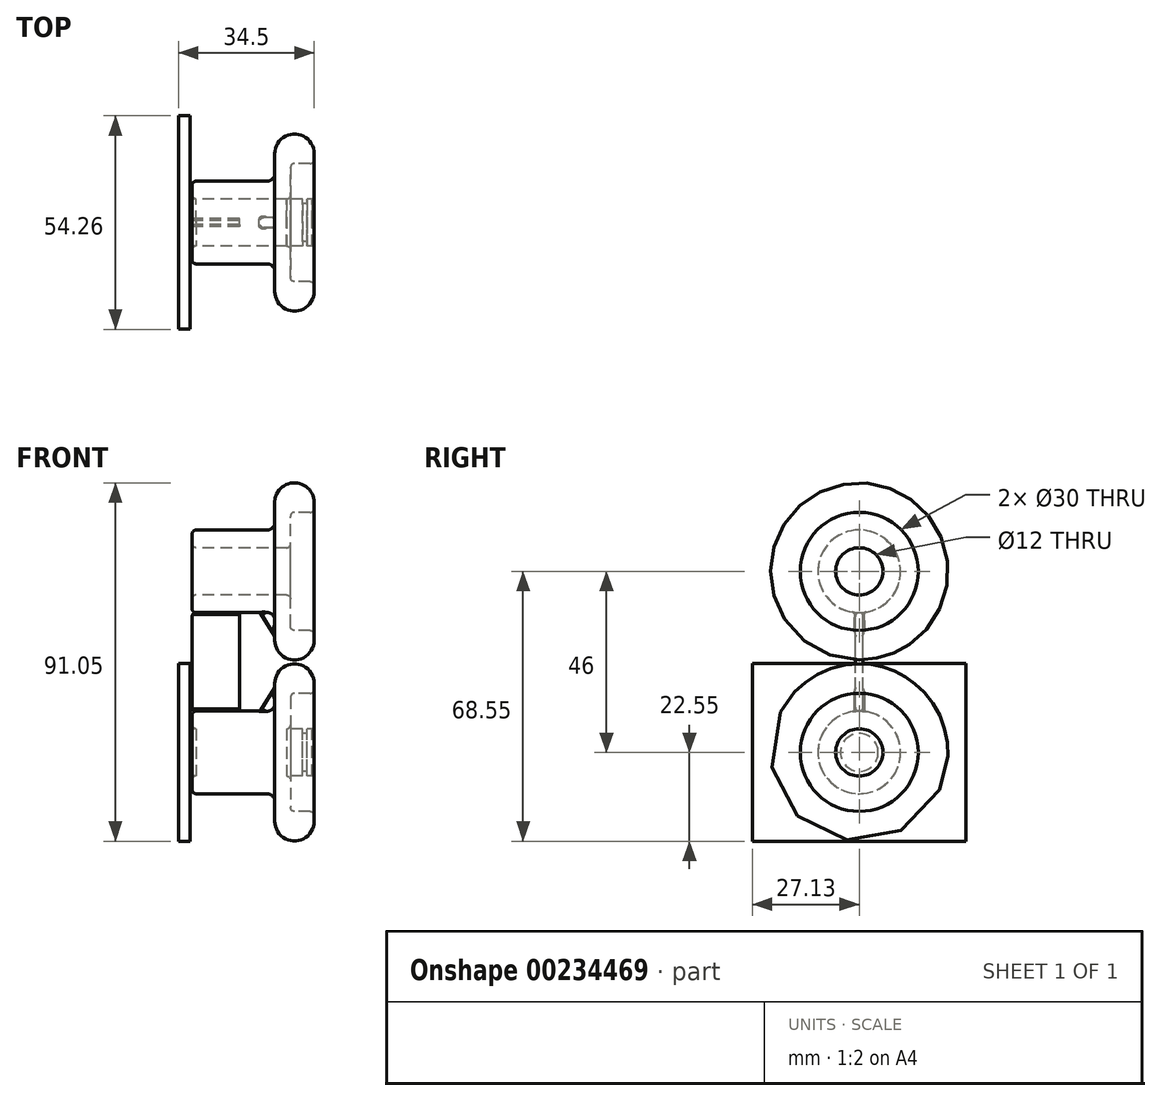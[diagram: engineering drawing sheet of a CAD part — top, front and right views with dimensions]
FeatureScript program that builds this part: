
annotation { "Feature Type Name" : "Feature", "Feature Type Description" : "" }
export const myFeature = defineFeature(function(context is Context, id is Id, definition is map)
    precondition{}
    {
        {
            var Q0;
            Q0=qCreatedBy(makeId("Right.planeOp"),FACE);
            var sketch = newSketch(context, id + "F0", { "sketchPlane" : qUnion([Q0])});
            skCircle(sketch, "E0", {"center": v(0, 0) * mm, "radius": 6 * mm});
            skSolve(sketch);
        }
        {
            var Q0;
            Q0 = qSketchRegion(id + "F0", true);
            extrude(context, id + "F1", {"entities" : qUnion([Q0]), "depth" : 31 * mm});
        }
        {
            var Q0;
            Q0=makeQuery(id+"F1.opExtrude","CAP_FACE",FACE,{"disambiguationData":[OSD([sQuery(id+"F0.wireOp",EDGE,"E0")])],"isStart":true});
            var sketch = newSketch(context, id + "F2", { "sketchPlane" : qUnion([Q0])});
            skLineSegment(sketch, "E1.bottom", {"start": v(-27.13, 22.55) * mm, "end": v(27.13, 22.55) * mm});
            skLineSegment(sketch, "E1.top", {"start": v(-27.13, -22.55) * mm, "end": v(27.13, -22.55) * mm});
            skLineSegment(sketch, "E1.left", {"start": v(-27.13, 22.55) * mm, "end": v(-27.13, -22.55) * mm});
            skLineSegment(sketch, "E1.right", {"start": v(27.13, 22.55) * mm, "end": v(27.13, -22.55) * mm});
            skPoint(sketch, "E1.middle", {"position": v(0, 0) * mm});
            skSolve(sketch);
        }
        {
            var Q0;
            Q0 = qSketchRegion(id + "F2", true);
            extrude(context, id + "F3", {"entities" : qUnion([Q0]), "operationType" : NewBodyOperationType.ADD, "depth" : 3 * mm});
        }
        {
            var Q0;
            Q0=qCreatedBy(makeId("Right.planeOp"),FACE);
            cPlane(context, id + "F4", {"entities" : qUnion([Q0]), "cplaneType" : CPlaneType.OFFSET, "offset" : 28.5 * mm, "width" : 150 * mm, "height" : 150 * mm});
        }
        {
            var Q0;
            Q0=qCreatedBy(id+"F4.planeOp",FACE);
            var sketch = newSketch(context, id + "F5", { "sketchPlane" : qUnion([Q0])});
            skCircle(sketch, "E2.0", {"center": v(0, 0) * mm, "radius": 6 * mm});
            skCircle(sketch, "E3", {"center": v(0, 0) * mm, "radius": 4.8 * mm});
            skSolve(sketch);
        }
        {
            var Q0;
            Q0 = qSketchRegion(id + "F5", true);
            extrude(context, id + "F6", {"entities" : qUnion([Q0]), "operationType" : NewBodyOperationType.REMOVE, "depth" : 1.2 * mm});
        }
        {
            var Q0;
            Q0=qCreatedBy(makeId("Front.planeOp"),FACE);
            var sketch = newSketch(context, id + "F7", { "sketchPlane" : qUnion([Q0])});
            skLineSegment(sketch, "E4", {"start": v(0.5, 6) * mm, "end": v(25.5, 6) * mm});
            skLineSegment(sketch, "E5", {"start": v(25.5, 6) * mm, "end": v(25.5, 15) * mm});
            skLineSegment(sketch, "E6", {"start": v(25.5, 15) * mm, "end": v(31.5, 15) * mm});
            skLineSegment(sketch, "E7", {"start": v(31.5, 15) * mm, "end": v(31.5, 17.5) * mm});
            skArc(sketch, "E8", {"start": v(31.5, 17.5) * mm, "mid": v(26.5, 22.5) * mm, "end": v(21.5, 17.5) * mm});
            skLineSegment(sketch, "E9", {"start": v(21.5, 17.5) * mm, "end": v(21.5, 10.5) * mm});
            skLineSegment(sketch, "E10", {"start": v(21.5, 10.5) * mm, "end": v(0.5, 10.5) * mm});
            skLineSegment(sketch, "E11", {"start": v(0.5, 10.5) * mm, "end": v(0.5, 6) * mm});
            skLineSegment(sketch, "E12", {"start": v(0, 0) * mm, "end": v(43.23, 0) * mm, "construction": true});
            skSolve(sketch);
        }
        {
            var Q0;
            Q0 = qSketchRegion(id + "F7", true);
            var Q1;
            Q1=sQuery(id+"F7.wireOp",EDGE,"E12");
            revolve(context, id + "F8", {"entities" : qUnion([Q0]), "axis" : qUnion([Q1]), "revolveType" : RevolveType.FULL});
        }
        {
            var Q0;
            Q0=qCreatedBy(makeId("Front.planeOp"),FACE);
            var sketch = newSketch(context, id + "F9", { "sketchPlane" : qUnion([Q0])});
            skLineSegment(sketch, "E13", {"start": v(17.5, 10.5) * mm, "end": v(21.5, 10.5) * mm, "construction": true});
            skLineSegment(sketch, "E14.0", {"start": v(21.5, 10.5) * mm, "end": v(21.5, 16.5) * mm});
            skPoint(sketch, "E15.orphan", {"position": v(21.5, 17.5) * mm});
            skPoint(sketch, "E16.orphan", {"position": v(21.5, -17.5) * mm});
            skLineSegment(sketch, "E17", {"start": v(17.5, 10.5) * mm, "end": v(17.5, 10) * mm, "construction": true});
            skLineSegment(sketch, "E18", {"start": v(17.5, 10) * mm, "end": v(21.5, 10) * mm});
            skLineSegment(sketch, "E19", {"start": v(21.5, 10) * mm, "end": v(21.5, 10.5) * mm});
            skLineSegment(sketch, "E20", {"start": v(21.5, 16.5) * mm, "end": v(17.5, 10) * mm});
            skSolve(sketch);
        }
        {
            var Q0;
            Q0 = qSketchRegion(id + "F9", true);
            extrude(context, id + "F10", {"entities" : qUnion([Q0]), "operationType" : NewBodyOperationType.ADD, "depth" : 2.5 * mm, "symmetric" : true});
        }
        {
            var Q0;
            Q0=makeQuery(id+"F8.opRevolve","SWEPT_EDGE",EDGE,{"disambiguationData":[OSD([sQuery(id+"F7.wireOp",EDGE,"E10"),sQuery(id+"F7.wireOp",EDGE,"E11")])]});
            var Q1;
            Q1=makeQuery(id+"F8.opRevolve","SWEPT_EDGE",EDGE,{"disambiguationData":[OSD([sQuery(id+"F7.wireOp",EDGE,"E6"),sQuery(id+"F7.wireOp",EDGE,"E7")])]});
            var Q2;
            Q2=makeQuery(id+"F8.opRevolve","SWEPT_EDGE",EDGE,{"disambiguationData":[OSD([sQuery(id+"F7.wireOp",EDGE,"E5"),sQuery(id+"F7.wireOp",EDGE,"E6")])]});
            var Q3;
            Q3=makeQuery(id+"F8.opRevolve","SWEPT_EDGE",EDGE,{"disambiguationData":[OSD([sQuery(id+"F7.wireOp",EDGE,"E4"),sQuery(id+"F7.wireOp",EDGE,"E5")])]});
            var Q4;
            Q4=makeQuery(id+"F8.opRevolve","SWEPT_EDGE",EDGE,{"disambiguationData":[OSD([sQuery(id+"F7.wireOp",EDGE,"E4"),sQuery(id+"F7.wireOp",EDGE,"E11")])]});
            fillet(context, id + "F11", {"entities" : qUnion([Q0, Q1, Q2, Q3, Q4]), "radius" : 1 * mm, "tangentPropagation" : true, "allowEdgeOverflow" : false});
        }
        {
            var Q0;
            {var subQ0=sQuery(id+"F7.wireOp",EDGE,"E9");var subQ2=sQuery(id+"F7.wireOp",EDGE,"E10");var subQ4=sQuery(id+"F9.wireOp",EDGE,"E19");var subQ5=sQuery(id+"F9.wireOp",EDGE,"E18");var subQ6=sQuery(id+"F9.wireOp",EDGE,"E17");var subQ7=sQuery(id+"F9.wireOp",EDGE,"57NRQQfy-ApiX-kUXl-zlCa-fPG9OK4gbSLN");var subQ8=sQuery(id+"F9.wireOp",EDGE,"E14.0");var subQ9=makeQuery(id+"FuQiQC3kxtkCGsf_2.5.F10.opExtrude","CAP_FACE",FACE,{"disambiguationData":[OSD([subQ8,subQ7,subQ6,subQ5,subQ4])],"isStart":true});var subQ10=makeQuery(id+"F10.opExtrude","CAP_FACE",FACE,{"disambiguationData":[OSD([subQ8,subQ7,subQ6,subQ5,subQ4])],"isStart":false});Q0=makeQuery(id+"FuQiQC3kxtkCGsf_2.6.F10.boolean.opBoolean","SPLIT",EDGE,{"disambiguationData":[TD([subQ9])],"derivedFrom":makeQuery(id+"FuQiQC3kxtkCGsf_2.5.F10.boolean.opBoolean","SPLIT",EDGE,{"disambiguationData":[TD([subQ10])],"derivedFrom":makeQuery(id+"FuQiQC3kxtkCGsf_2.4.F10.boolean.opBoolean","SPLIT",EDGE,{"disambiguationData":[TD([subQ10])],"derivedFrom":makeQuery(id+"FuQiQC3kxtkCGsf_2.3.F10.boolean.opBoolean","SPLIT",EDGE,{"disambiguationData":[TD([subQ10])],"derivedFrom":makeQuery(id+"FuQiQC3kxtkCGsf_2.2.F10.boolean.opBoolean","SPLIT",EDGE,{"disambiguationData":[TD([subQ10])],"derivedFrom":makeQuery(id+"FuQiQC3kxtkCGsf_2.1.F10.boolean.opBoolean","SPLIT",EDGE,{"disambiguationData":[TD([subQ10])],"derivedFrom":makeQuery(id+"F8.opRevolve","SWEPT_EDGE",EDGE,{"disambiguationData":[OSD([subQ0,subQ2])]})})})})})})});}
            var Q1;
            {var subQ0=sQuery(id+"F7.wireOp",EDGE,"E9");var subQ2=sQuery(id+"F7.wireOp",EDGE,"E10");var subQ4=sQuery(id+"F9.wireOp",EDGE,"E19");var subQ5=sQuery(id+"F9.wireOp",EDGE,"E18");var subQ6=sQuery(id+"F9.wireOp",EDGE,"E17");var subQ7=sQuery(id+"F9.wireOp",EDGE,"57NRQQfy-ApiX-kUXl-zlCa-fPG9OK4gbSLN");var subQ8=sQuery(id+"F9.wireOp",EDGE,"E14.0");var subQ9=makeQuery(id+"FuQiQC3kxtkCGsf_2.6.F10.opExtrude","CAP_FACE",FACE,{"disambiguationData":[OSD([subQ8,subQ7,subQ6,subQ5,subQ4])],"isStart":true});var subQ10=makeQuery(id+"F10.opExtrude","CAP_FACE",FACE,{"disambiguationData":[OSD([subQ8,subQ7,subQ6,subQ5,subQ4])],"isStart":false});Q1=makeQuery(id+"FuQiQC3kxtkCGsf_2.7.F10.boolean.opBoolean","SPLIT",EDGE,{"disambiguationData":[TD([subQ9])],"derivedFrom":makeQuery(id+"FuQiQC3kxtkCGsf_2.6.F10.boolean.opBoolean","SPLIT",EDGE,{"disambiguationData":[TD([subQ10])],"derivedFrom":makeQuery(id+"FuQiQC3kxtkCGsf_2.5.F10.boolean.opBoolean","SPLIT",EDGE,{"disambiguationData":[TD([subQ10])],"derivedFrom":makeQuery(id+"FuQiQC3kxtkCGsf_2.4.F10.boolean.opBoolean","SPLIT",EDGE,{"disambiguationData":[TD([subQ10])],"derivedFrom":makeQuery(id+"FuQiQC3kxtkCGsf_2.3.F10.boolean.opBoolean","SPLIT",EDGE,{"disambiguationData":[TD([subQ10])],"derivedFrom":makeQuery(id+"FuQiQC3kxtkCGsf_2.2.F10.boolean.opBoolean","SPLIT",EDGE,{"disambiguationData":[TD([subQ10])],"derivedFrom":makeQuery(id+"FuQiQC3kxtkCGsf_2.1.F10.boolean.opBoolean","SPLIT",EDGE,{"disambiguationData":[TD([subQ10])],"derivedFrom":makeQuery(id+"F8.opRevolve","SWEPT_EDGE",EDGE,{"disambiguationData":[OSD([subQ0,subQ2])]})})})})})})})});}
            var Q2;
            {var subQ0=sQuery(id+"F7.wireOp",EDGE,"E9");var subQ2=sQuery(id+"F7.wireOp",EDGE,"E10");var subQ4=sQuery(id+"F9.wireOp",EDGE,"E19");var subQ5=sQuery(id+"F9.wireOp",EDGE,"E18");var subQ6=sQuery(id+"F9.wireOp",EDGE,"E17");var subQ7=sQuery(id+"F9.wireOp",EDGE,"57NRQQfy-ApiX-kUXl-zlCa-fPG9OK4gbSLN");var subQ8=sQuery(id+"F9.wireOp",EDGE,"E14.0");var subQ9=makeQuery(id+"FuQiQC3kxtkCGsf_2.4.F10.opExtrude","CAP_FACE",FACE,{"disambiguationData":[OSD([subQ8,subQ7,subQ6,subQ5,subQ4])],"isStart":true});var subQ10=makeQuery(id+"F10.opExtrude","CAP_FACE",FACE,{"disambiguationData":[OSD([subQ8,subQ7,subQ6,subQ5,subQ4])],"isStart":false});Q2=makeQuery(id+"FuQiQC3kxtkCGsf_2.5.F10.boolean.opBoolean","SPLIT",EDGE,{"disambiguationData":[TD([subQ9])],"derivedFrom":makeQuery(id+"FuQiQC3kxtkCGsf_2.4.F10.boolean.opBoolean","SPLIT",EDGE,{"disambiguationData":[TD([subQ10])],"derivedFrom":makeQuery(id+"FuQiQC3kxtkCGsf_2.3.F10.boolean.opBoolean","SPLIT",EDGE,{"disambiguationData":[TD([subQ10])],"derivedFrom":makeQuery(id+"FuQiQC3kxtkCGsf_2.2.F10.boolean.opBoolean","SPLIT",EDGE,{"disambiguationData":[TD([subQ10])],"derivedFrom":makeQuery(id+"FuQiQC3kxtkCGsf_2.1.F10.boolean.opBoolean","SPLIT",EDGE,{"disambiguationData":[TD([subQ10])],"derivedFrom":makeQuery(id+"F8.opRevolve","SWEPT_EDGE",EDGE,{"disambiguationData":[OSD([subQ0,subQ2])]})})})})})});}
            var Q3;
            {var subQ0=sQuery(id+"F7.wireOp",EDGE,"E9");var subQ2=sQuery(id+"F9.wireOp",EDGE,"E19");var subQ3=sQuery(id+"F9.wireOp",EDGE,"E18");var subQ4=sQuery(id+"F9.wireOp",EDGE,"E17");var subQ5=sQuery(id+"F9.wireOp",EDGE,"57NRQQfy-ApiX-kUXl-zlCa-fPG9OK4gbSLN");var subQ6=sQuery(id+"F9.wireOp",EDGE,"E14.0");var subQ7=makeQuery(id+"FuQiQC3kxtkCGsf_2.3.F10.opExtrude","CAP_FACE",FACE,{"disambiguationData":[OSD([subQ6,subQ5,subQ4,subQ3,subQ2])],"isStart":true});var subQ8=sQuery(id+"F7.wireOp",EDGE,"E10");var subQ10=makeQuery(id+"F10.opExtrude","CAP_FACE",FACE,{"disambiguationData":[OSD([subQ6,subQ5,subQ4,subQ3,subQ2])],"isStart":false});Q3=makeQuery(id+"FuQiQC3kxtkCGsf_2.4.F10.boolean.opBoolean","SPLIT",EDGE,{"disambiguationData":[TD([subQ7])],"derivedFrom":makeQuery(id+"FuQiQC3kxtkCGsf_2.3.F10.boolean.opBoolean","SPLIT",EDGE,{"disambiguationData":[TD([subQ10])],"derivedFrom":makeQuery(id+"FuQiQC3kxtkCGsf_2.2.F10.boolean.opBoolean","SPLIT",EDGE,{"disambiguationData":[TD([subQ10])],"derivedFrom":makeQuery(id+"FuQiQC3kxtkCGsf_2.1.F10.boolean.opBoolean","SPLIT",EDGE,{"disambiguationData":[TD([subQ10])],"derivedFrom":makeQuery(id+"F8.opRevolve","SWEPT_EDGE",EDGE,{"disambiguationData":[OSD([subQ0,subQ8])]})})})})});}
            var Q4;
            {var subQ0=sQuery(id+"F7.wireOp",EDGE,"E9");var subQ2=sQuery(id+"F9.wireOp",EDGE,"E19");var subQ3=sQuery(id+"F9.wireOp",EDGE,"E18");var subQ4=sQuery(id+"F9.wireOp",EDGE,"E17");var subQ5=sQuery(id+"F9.wireOp",EDGE,"57NRQQfy-ApiX-kUXl-zlCa-fPG9OK4gbSLN");var subQ6=sQuery(id+"F9.wireOp",EDGE,"E14.0");var subQ7=makeQuery(id+"FuQiQC3kxtkCGsf_2.2.F10.opExtrude","CAP_FACE",FACE,{"disambiguationData":[OSD([subQ6,subQ5,subQ4,subQ3,subQ2])],"isStart":true});var subQ8=sQuery(id+"F7.wireOp",EDGE,"E10");var subQ10=makeQuery(id+"F10.opExtrude","CAP_FACE",FACE,{"disambiguationData":[OSD([subQ6,subQ5,subQ4,subQ3,subQ2])],"isStart":false});Q4=makeQuery(id+"FuQiQC3kxtkCGsf_2.3.F10.boolean.opBoolean","SPLIT",EDGE,{"disambiguationData":[TD([subQ7])],"derivedFrom":makeQuery(id+"FuQiQC3kxtkCGsf_2.2.F10.boolean.opBoolean","SPLIT",EDGE,{"disambiguationData":[TD([subQ10])],"derivedFrom":makeQuery(id+"FuQiQC3kxtkCGsf_2.1.F10.boolean.opBoolean","SPLIT",EDGE,{"disambiguationData":[TD([subQ10])],"derivedFrom":makeQuery(id+"F8.opRevolve","SWEPT_EDGE",EDGE,{"disambiguationData":[OSD([subQ0,subQ8])]})})})});}
            var Q5;
            {var subQ0=sQuery(id+"F7.wireOp",EDGE,"E9");var subQ2=sQuery(id+"F7.wireOp",EDGE,"E10");var subQ4=sQuery(id+"F9.wireOp",EDGE,"E19");var subQ5=sQuery(id+"F9.wireOp",EDGE,"E18");var subQ6=sQuery(id+"F9.wireOp",EDGE,"E17");var subQ7=sQuery(id+"F9.wireOp",EDGE,"57NRQQfy-ApiX-kUXl-zlCa-fPG9OK4gbSLN");var subQ8=sQuery(id+"F9.wireOp",EDGE,"E14.0");var subQ9=makeQuery(id+"FuQiQC3kxtkCGsf_2.1.F10.opExtrude","CAP_FACE",FACE,{"disambiguationData":[OSD([subQ8,subQ7,subQ6,subQ5,subQ4])],"isStart":true});Q5=makeQuery(id+"FuQiQC3kxtkCGsf_2.2.F10.boolean.opBoolean","SPLIT",EDGE,{"disambiguationData":[TD([subQ9])],"derivedFrom":makeQuery(id+"FuQiQC3kxtkCGsf_2.1.F10.boolean.opBoolean","SPLIT",EDGE,{"disambiguationData":[TD([makeQuery(id+"F10.opExtrude","CAP_FACE",FACE,{"disambiguationData":[OSD([subQ8,subQ7,subQ6,subQ5,subQ4])],"isStart":false})])],"derivedFrom":makeQuery(id+"F8.opRevolve","SWEPT_EDGE",EDGE,{"disambiguationData":[OSD([subQ0,subQ2])]})})});}
            var Q6;
            {var subQ0=sQuery(id+"F7.wireOp",EDGE,"E9");var subQ1=sQuery(id+"F9.wireOp",EDGE,"E19");var subQ2=sQuery(id+"F9.wireOp",EDGE,"E18");var subQ3=sQuery(id+"F9.wireOp",EDGE,"E17");var subQ4=sQuery(id+"F9.wireOp",EDGE,"57NRQQfy-ApiX-kUXl-zlCa-fPG9OK4gbSLN");var subQ5=sQuery(id+"F9.wireOp",EDGE,"E14.0");var subQ6=sQuery(id+"F7.wireOp",EDGE,"E10");Q6=makeQuery(id+"FuQiQC3kxtkCGsf_2.1.F10.boolean.opBoolean","SPLIT",EDGE,{"disambiguationData":[TD([makeQuery(id+"F10.opExtrude","CAP_FACE",FACE,{"disambiguationData":[OSD([subQ5,subQ4,subQ3,subQ2,subQ1])],"isStart":true})])],"derivedFrom":makeQuery(id+"F8.opRevolve","SWEPT_EDGE",EDGE,{"disambiguationData":[OSD([subQ0,subQ6])]})});}
            var Q7;
            {var subQ0=sQuery(id+"F7.wireOp",EDGE,"E9");var subQ2=sQuery(id+"F7.wireOp",EDGE,"E10");var subQ4=sQuery(id+"F9.wireOp",EDGE,"E19");var subQ5=sQuery(id+"F9.wireOp",EDGE,"E18");var subQ6=sQuery(id+"F9.wireOp",EDGE,"E17");var subQ7=sQuery(id+"F9.wireOp",EDGE,"57NRQQfy-ApiX-kUXl-zlCa-fPG9OK4gbSLN");var subQ8=sQuery(id+"F9.wireOp",EDGE,"E14.0");var subQ9=makeQuery(id+"F10.opExtrude","CAP_FACE",FACE,{"disambiguationData":[OSD([subQ8,subQ7,subQ6,subQ5,subQ4])],"isStart":false});Q7=makeQuery(id+"FuQiQC3kxtkCGsf_2.7.F10.boolean.opBoolean","SPLIT",EDGE,{"disambiguationData":[TD([subQ9])],"derivedFrom":makeQuery(id+"FuQiQC3kxtkCGsf_2.6.F10.boolean.opBoolean","SPLIT",EDGE,{"disambiguationData":[TD([subQ9])],"derivedFrom":makeQuery(id+"FuQiQC3kxtkCGsf_2.5.F10.boolean.opBoolean","SPLIT",EDGE,{"disambiguationData":[TD([subQ9])],"derivedFrom":makeQuery(id+"FuQiQC3kxtkCGsf_2.4.F10.boolean.opBoolean","SPLIT",EDGE,{"disambiguationData":[TD([subQ9])],"derivedFrom":makeQuery(id+"FuQiQC3kxtkCGsf_2.3.F10.boolean.opBoolean","SPLIT",EDGE,{"disambiguationData":[TD([subQ9])],"derivedFrom":makeQuery(id+"FuQiQC3kxtkCGsf_2.2.F10.boolean.opBoolean","SPLIT",EDGE,{"disambiguationData":[TD([subQ9])],"derivedFrom":makeQuery(id+"FuQiQC3kxtkCGsf_2.1.F10.boolean.opBoolean","SPLIT",EDGE,{"disambiguationData":[TD([subQ9])],"derivedFrom":makeQuery(id+"F8.opRevolve","SWEPT_EDGE",EDGE,{"disambiguationData":[OSD([subQ0,subQ2])]})})})})})})})});}
            fillet(context, id + "F12", {"entities" : qUnion([Q0, Q1, Q2, Q3, Q4, Q5, Q6, Q7]), "radius" : 2 * mm, "tangentPropagation" : true, "allowEdgeOverflow" : false});
        }
        {
            var Q0;
            Q0=makeQuery(id+"F10.opExtrude","SWEPT_FACE",FACE,{"disambiguationData":[OSD([sQuery(id+"F9.wireOp",EDGE,"E20")])]});
            var Q1;
            Q1=makeQuery(id+"FuQiQC3kxtkCGsf_2.7.F10.opExtrude","SWEPT_FACE",FACE,{"disambiguationData":[OSD([sQuery(id+"F9.wireOp",EDGE,"E20")])]});
            var Q2;
            Q2=makeQuery(id+"FuQiQC3kxtkCGsf_2.6.F10.opExtrude","SWEPT_FACE",FACE,{"disambiguationData":[OSD([sQuery(id+"F9.wireOp",EDGE,"E20")])]});
            var Q3;
            Q3=makeQuery(id+"FuQiQC3kxtkCGsf_2.5.F10.opExtrude","SWEPT_FACE",FACE,{"disambiguationData":[OSD([sQuery(id+"F9.wireOp",EDGE,"E20")])]});
            var Q4;
            Q4=makeQuery(id+"FuQiQC3kxtkCGsf_2.4.F10.opExtrude","SWEPT_FACE",FACE,{"disambiguationData":[OSD([sQuery(id+"F9.wireOp",EDGE,"E20")])]});
            var Q5;
            Q5=makeQuery(id+"FuQiQC3kxtkCGsf_2.3.F10.opExtrude","SWEPT_FACE",FACE,{"disambiguationData":[OSD([sQuery(id+"F9.wireOp",EDGE,"E20")])]});
            var Q6;
            Q6=makeQuery(id+"FuQiQC3kxtkCGsf_2.2.F10.opExtrude","SWEPT_FACE",FACE,{"disambiguationData":[OSD([sQuery(id+"F9.wireOp",EDGE,"E20")])]});
            var Q7;
            Q7=makeQuery(id+"FuQiQC3kxtkCGsf_2.1.F10.opExtrude","SWEPT_FACE",FACE,{"disambiguationData":[OSD([sQuery(id+"F9.wireOp",EDGE,"E20")])]});
            fillet(context, id + "F13", {"entities" : qUnion([Q0, Q1, Q2, Q3, Q4, Q5, Q6, Q7]), "radius" : 0.5 * mm, "tangentPropagation" : true, "allowEdgeOverflow" : false});
        }
        {
            var Q0;
            Q0=qCreatedBy(makeId("Top.planeOp"),FACE);
            cPlane(context, id + "F14", {"entities" : qUnion([Q0]), "cplaneType" : CPlaneType.OFFSET, "offset" : 23 * mm, "width" : 150 * mm, "height" : 150 * mm});
        }
        {
            var Q0;
            Q0=makeQuery(id+"F8.opRevolve","SWEPT_BODY",BODY,{"disambiguationData":[OSD([sQuery(id+"F7.wireOp",EDGE,"E4"),sQuery(id+"F7.wireOp",EDGE,"E5"),sQuery(id+"F7.wireOp",EDGE,"E6"),sQuery(id+"F7.wireOp",EDGE,"E7"),sQuery(id+"F7.wireOp",EDGE,"E8"),sQuery(id+"F7.wireOp",EDGE,"E9"),sQuery(id+"F7.wireOp",EDGE,"E10"),sQuery(id+"F7.wireOp",EDGE,"E11")])]});
            var Q1;
            Q1=qCreatedBy(id+"F14.planeOp",FACE);
            mirror(context, id + "F15", {"operationType" : NewBodyOperationType.ADD, "entities" : qUnion([Q0]), "mirrorPlane" : qUnion([Q1])});
        }
        {
            var Q0;
            Q0=makeQuery(id+"F8.opRevolve","SWEPT_FACE",FACE,{"disambiguationData":[OSD([sQuery(id+"F7.wireOp",EDGE,"E11")])]});
            var sketch = newSketch(context, id + "F16", { "sketchPlane" : qUnion([Q0])});
            skArc(sketch, "E21.0", {"start": v(0.5, 10.49) * mm, "mid": v(0, 10.5) * mm, "end": v(-0.5, 10.49) * mm});
            skArc(sketch, "E22.0", {"start": v(-0.5, 35.51) * mm, "mid": v(0, 35.5) * mm, "end": v(0.5, 35.51) * mm});
            skLineSegment(sketch, "E23", {"start": v(-0.5, 10.49) * mm, "end": v(-0.5, 35.51) * mm, "construction": true});
            skLineSegment(sketch, "E24", {"start": v(0.5, 35.51) * mm, "end": v(0.5, 10.49) * mm, "construction": true});
            skLineSegment(sketch, "E25", {"start": v(-1, 10.99) * mm, "end": v(-1, 35.01) * mm});
            skLineSegment(sketch, "E26", {"start": v(-0.5, 10.49) * mm, "end": v(-1, 10.99) * mm});
            skLineSegment(sketch, "E27", {"start": v(-1, 35.01) * mm, "end": v(-0.5, 35.51) * mm});
            skLineSegment(sketch, "E28.MirrorCS", {"start": v(1, 35.01) * mm, "end": v(0.5, 35.51) * mm});
            skLineSegment(sketch, "E29.MirrorCS", {"start": v(0.5, 10.49) * mm, "end": v(1, 10.99) * mm});
            skLineSegment(sketch, "E30.MirrorCS", {"start": v(1, 10.99) * mm, "end": v(1, 35.01) * mm});
            skSolve(sketch);
        }
        {
            var Q0;
            Q0 = qSketchRegion(id + "F16", true);
            extrude(context, id + "F17", {"entities" : qUnion([Q0]), "operationType" : NewBodyOperationType.ADD, "oppositeDirection" : true, "depth" : 12 * mm});
        }
        {
            var Q0;
            Q0=makeQuery(id+"F17.opExtrude","CAP_EDGE",EDGE,{"disambiguationData":[OSD([sQuery(id+"F16.wireOp",EDGE,"E21.0")])],"isStart":true});
            var Q1;
            Q1=makeQuery(id+"F17.opExtrude","CAP_EDGE",EDGE,{"disambiguationData":[OSD([sQuery(id+"F16.wireOp",EDGE,"E22.0")])],"isStart":true});
            fillet(context, id + "F18", {"entities" : qUnion([Q0, Q1]), "radius" : 1 * mm, "tangentPropagation" : true, "allowEdgeOverflow" : false});
        }
    });
